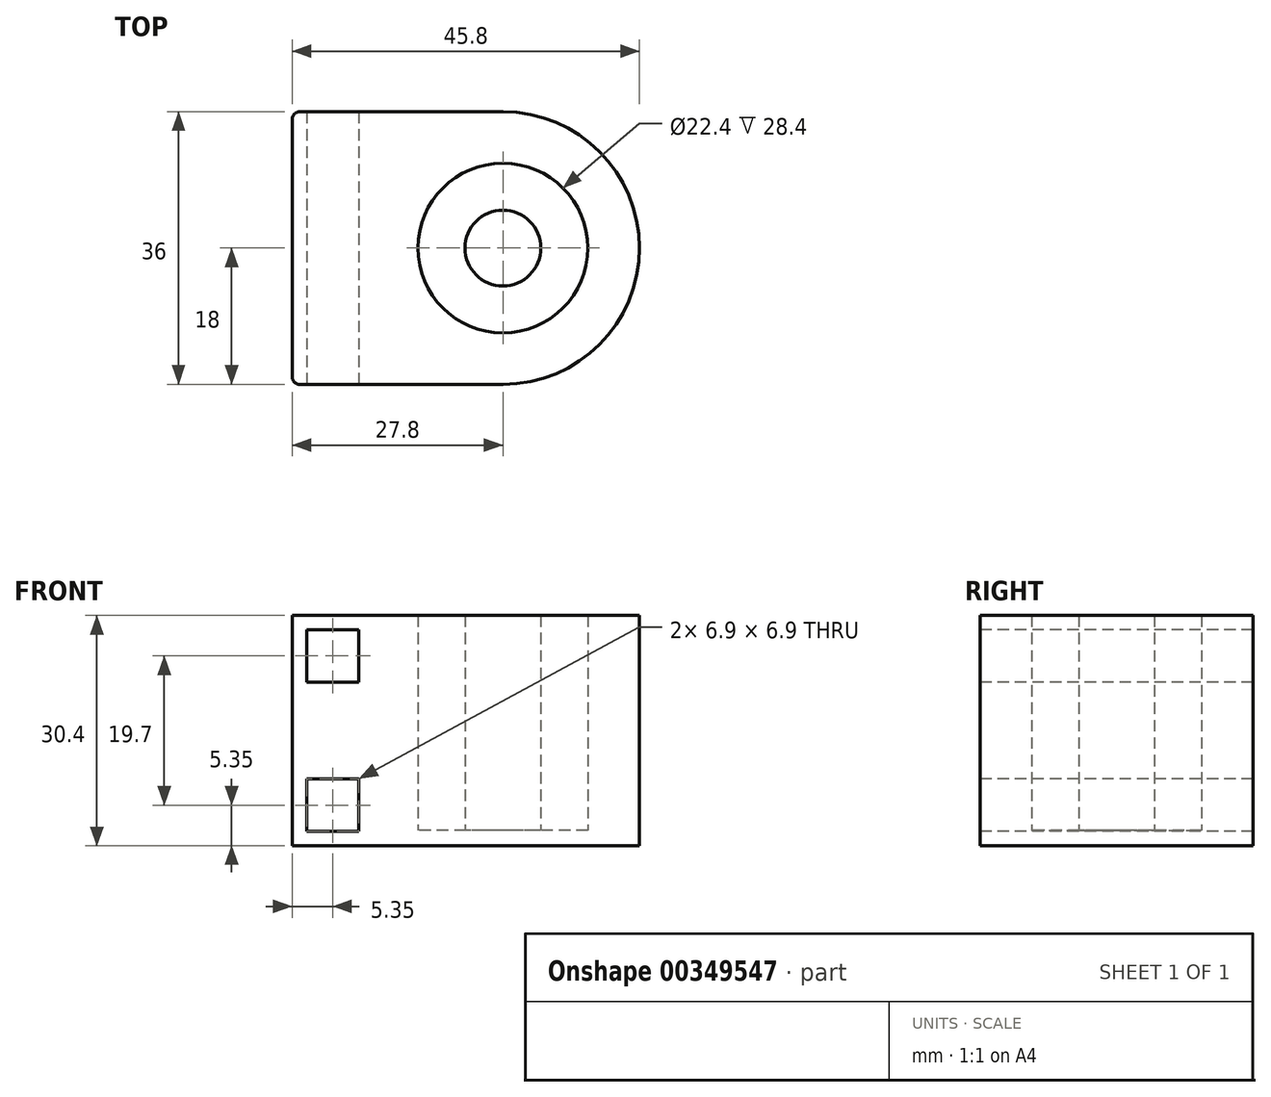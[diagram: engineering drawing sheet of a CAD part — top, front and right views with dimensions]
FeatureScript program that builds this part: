
annotation { "Feature Type Name" : "Feature", "Feature Type Description" : "" }
export const myFeature = defineFeature(function(context is Context, id is Id, definition is map)
    precondition{}
    {
        {
            var Q0;
            Q0=qCreatedBy(makeId("Top.planeOp"),FACE);
            var sketch = newSketch(context, id + "F0", { "sketchPlane" : qUnion([Q0])});
            skCircle(sketch, "E0", {"center": v(0, 0) * mm, "radius": 11.2 * mm});
            skCircle(sketch, "E1", {"center": v(0, 0) * mm, "radius": 18 * mm});
            skLineSegment(sketch, "E2", {"start": v(0, 0) * mm, "end": v(0, 18) * mm});
            skLineSegment(sketch, "E3.bottom", {"start": v(0, 18) * mm, "end": v(-27.8, 18) * mm});
            skLineSegment(sketch, "E3.top", {"start": v(0, -18) * mm, "end": v(-27.8, -18) * mm});
            skLineSegment(sketch, "E3.left", {"start": v(0, 18) * mm, "end": v(0, -18) * mm});
            skLineSegment(sketch, "E3.right", {"start": v(-27.8, 18) * mm, "end": v(-27.8, -18) * mm});
            skCircle(sketch, "E4", {"center": v(0, 0) * mm, "radius": 5 * mm});
            skSolve(sketch);
        }
        {
            var Q0;
            {var subQ1=sQuery(id+"F0.wireOp",EDGE,"E3.bottom");Q0=makeQuery(id+"F0.imprint","IMPRINT",FACE,{"disambiguationData":[TD([[makeQuery(id+"F0.imprint","IMPRINT",EDGE,{"derivedFrom":subQ1}),1.0]])]});}
            var Q1;
            {var subQ0=sQuery(id+"F0.wireOp",EDGE,"E3.left");var subQ1=sQuery(id+"F0.wireOp",EDGE,"E0");var subQ2=makeQuery(id+"F0.imprint","INTERSECT",VERTEX,{"disambiguationData":[OD(0.0)],"derivedFrom":[subQ1,subQ0]});Q1=makeQuery(id+"F0.imprint","IMPRINT",FACE,{"disambiguationData":[TD([[makeQuery(id+"F0.imprint","IMPRINT",EDGE,{"disambiguationData":[TD([[subQ2,-1.0]])],"derivedFrom":subQ1}),-1.0]])]});}
            var Q2;
            {var subQ0=sQuery(id+"F0.wireOp",EDGE,"E3.left");var subQ1=sQuery(id+"F0.wireOp",EDGE,"E0");var subQ2=makeQuery(id+"F0.imprint","INTERSECT",VERTEX,{"disambiguationData":[OD(0.0)],"derivedFrom":[subQ1,subQ0]});Q2=makeQuery(id+"F0.imprint","IMPRINT",FACE,{"disambiguationData":[TD([[makeQuery(id+"F0.imprint","IMPRINT",EDGE,{"disambiguationData":[TD([[subQ2,1.0]])],"derivedFrom":subQ1}),-1.0]])]});}
            extrude(context, id + "F1", {"entities" : qUnion([Q0, Q1, Q2]), "depth" : 30.4 * mm});
        }
        {
            var Q0;
            {var subQ5=sQuery(id+"F0.wireOp",EDGE,"E3.left");var subQ6=sQuery(id+"F0.wireOp",EDGE,"E0");var subQ7=makeQuery(id+"F0.imprint","INTERSECT",VERTEX,{"disambiguationData":[OD(0.0)],"derivedFrom":[subQ6,subQ5]});Q0=makeQuery(id+"F0.imprint","IMPRINT",FACE,{"disambiguationData":[TD([[makeQuery(id+"F0.imprint","IMPRINT",EDGE,{"disambiguationData":[TD([[subQ7,1.0]])],"derivedFrom":subQ6}),1.0]])]});}
            var Q1;
            {var subQ12=sQuery(id+"F0.wireOp",EDGE,"E3.left");var subQ13=sQuery(id+"F0.wireOp",EDGE,"E0");var subQ14=makeQuery(id+"F0.imprint","INTERSECT",VERTEX,{"disambiguationData":[OD(0.0)],"derivedFrom":[subQ13,subQ12]});Q1=makeQuery(id+"F0.imprint","IMPRINT",FACE,{"disambiguationData":[TD([[makeQuery(id+"F0.imprint","IMPRINT",EDGE,{"disambiguationData":[TD([[subQ14,-1.0]])],"derivedFrom":subQ13}),1.0]])]});}
            var Q2;
            {var subQ0=sQuery(id+"F0.wireOp",EDGE,"8lIcankL-Q5gj-hwWK-AL3X-qkDdrb8kB20Y");var subQ1=sQuery(id+"F0.wireOp",EDGE,"E3.left");var subQ2=makeQuery(id+"F0.imprint","INTERSECT",VERTEX,{"disambiguationData":[OD(1.0)],"derivedFrom":[subQ1,subQ0]});Q2=makeQuery(id+"F0.imprint","IMPRINT",FACE,{"disambiguationData":[TD([[makeQuery(id+"F0.imprint","IMPRINT",EDGE,{"disambiguationData":[TD([[subQ2,-1.0]])],"derivedFrom":subQ1}),-1.0]])]});}
            var Q3;
            {var subQ0=sQuery(id+"F0.wireOp",EDGE,"8lIcankL-Q5gj-hwWK-AL3X-qkDdrb8kB20Y");var subQ1=sQuery(id+"F0.wireOp",EDGE,"E3.left");var subQ2=makeQuery(id+"F0.imprint","INTERSECT",VERTEX,{"disambiguationData":[OD(1.0)],"derivedFrom":[subQ1,subQ0]});Q3=makeQuery(id+"F0.imprint","IMPRINT",FACE,{"disambiguationData":[TD([[makeQuery(id+"F0.imprint","IMPRINT",EDGE,{"disambiguationData":[TD([[subQ2,-1.0]])],"derivedFrom":subQ1}),1.0]])]});}
            var Q4;
            {var subQ0=sQuery(id+"F0.wireOp",EDGE,"acbbde6d-6b89-4c3b-ba40-6ba3c0975178.1");var subQ1=sQuery(id+"F0.wireOp",EDGE,"E4");var subQ2=makeQuery(id+"F0.imprint","INTERSECT",VERTEX,{"disambiguationData":[OD(1.0)],"derivedFrom":[subQ1,subQ0]});Q4=makeQuery(id+"F0.imprint","IMPRINT",FACE,{"disambiguationData":[TD([[makeQuery(id+"F0.imprint","IMPRINT",EDGE,{"disambiguationData":[TD([[subQ2,-1.0]])],"derivedFrom":subQ1}),-1.0]])]});}
            var Q5;
            {var subQ0=sQuery(id+"F0.wireOp",EDGE,"acbbde6d-6b89-4c3b-ba40-6ba3c0975178.2");var subQ1=sQuery(id+"F0.wireOp",EDGE,"E4");var subQ2=makeQuery(id+"F0.imprint","INTERSECT",VERTEX,{"disambiguationData":[OD(1.0)],"derivedFrom":[subQ1,subQ0]});Q5=makeQuery(id+"F0.imprint","IMPRINT",FACE,{"disambiguationData":[TD([[makeQuery(id+"F0.imprint","IMPRINT",EDGE,{"disambiguationData":[TD([[subQ2,1.0]])],"derivedFrom":subQ1}),-1.0]])]});}
            var Q6;
            {var subQ0=sQuery(id+"F0.wireOp",EDGE,"E4");var subQ1=sQuery(id+"F0.wireOp",EDGE,"E3.left");var subQ2=makeQuery(id+"F0.imprint","INTERSECT",VERTEX,{"disambiguationData":[OD(1.0)],"derivedFrom":[subQ1,subQ0]});Q6=makeQuery(id+"F0.imprint","IMPRINT",FACE,{"disambiguationData":[TD([[makeQuery(id+"F0.imprint","IMPRINT",EDGE,{"disambiguationData":[TD([[subQ2,-1.0]])],"derivedFrom":subQ1}),1.0]])]});}
            var Q7;
            {var subQ0=sQuery(id+"F0.wireOp",EDGE,"E4");var subQ1=sQuery(id+"F0.wireOp",EDGE,"E3.left");var subQ2=makeQuery(id+"F0.imprint","INTERSECT",VERTEX,{"disambiguationData":[OD(1.0)],"derivedFrom":[subQ1,subQ0]});Q7=makeQuery(id+"F0.imprint","IMPRINT",FACE,{"disambiguationData":[TD([[makeQuery(id+"F0.imprint","IMPRINT",EDGE,{"disambiguationData":[TD([[subQ2,-1.0]])],"derivedFrom":subQ1}),-1.0]])]});}
            extrude(context, id + "F2", {"entities" : qUnion([Q0, Q1, Q2, Q3, Q4, Q5, Q6, Q7]), "operationType" : NewBodyOperationType.ADD, "depth" : 2 * mm});
        }
        {
            var Q0;
            Q0=makeQuery(id+"F1.opExtrude","SWEPT_FACE",FACE,{"disambiguationData":[OSD([sQuery(id+"F0.wireOp",EDGE,"E3.top")])]});
            var sketch = newSketch(context, id + "F3", { "sketchPlane" : qUnion([Q0])});
            skLineSegment(sketch, "E5.bottom", {"start": v(-27.8, 30.4) * mm, "end": v(-25.9, 30.4) * mm});
            skLineSegment(sketch, "E5.top", {"start": v(-27.8, 28.5) * mm, "end": v(-25.9, 28.5) * mm});
            skLineSegment(sketch, "E5.left", {"start": v(-27.8, 30.4) * mm, "end": v(-27.8, 28.5) * mm});
            skLineSegment(sketch, "E5.right", {"start": v(-25.9, 30.4) * mm, "end": v(-25.9, 28.5) * mm});
            skLineSegment(sketch, "E6.bottom", {"start": v(-25.9, 28.5) * mm, "end": v(-19, 28.5) * mm});
            skLineSegment(sketch, "E6.top", {"start": v(-25.9, 21.6) * mm, "end": v(-19, 21.6) * mm});
            skLineSegment(sketch, "E6.left", {"start": v(-25.9, 28.5) * mm, "end": v(-25.9, 21.6) * mm});
            skLineSegment(sketch, "E6.right", {"start": v(-19, 28.5) * mm, "end": v(-19, 21.6) * mm});
            skPoint(sketch, "E7", {"position": v(-27.8, 15.2) * mm});
            skLineSegment(sketch, "E8", {"start": v(-27.8, 15.2) * mm, "end": v(0, 15.2) * mm});
            skLineSegment(sketch, "E9.MirrorCS", {"start": v(-25.9, 8.8) * mm, "end": v(-19, 8.8) * mm});
            skLineSegment(sketch, "E10.MirrorCS", {"start": v(-19, 1.9) * mm, "end": v(-19, 8.8) * mm});
            skLineSegment(sketch, "E11.MirrorCS", {"start": v(-25.9, 1.9) * mm, "end": v(-19, 1.9) * mm});
            skLineSegment(sketch, "E12.MirrorCS", {"start": v(-25.9, 1.9) * mm, "end": v(-25.9, 8.8) * mm});
            skSolve(sketch);
        }
        {
            var Q0;
            Q0=makeQuery(id+"F3.imprint","IMPRINT",FACE,{"disambiguationData":[TD([[makeQuery(id+"F3.imprint","IMPRINT",EDGE,{"derivedFrom":sQuery(id+"F3.wireOp",EDGE,"E6.bottom")}),-1.0]])]});
            var Q1;
            Q1=makeQuery(id+"F3.imprint","IMPRINT",FACE,{"disambiguationData":[TD([[makeQuery(id+"F3.imprint","IMPRINT",EDGE,{"derivedFrom":sQuery(id+"F3.wireOp",EDGE,"E9.MirrorCS")}),-1.0]])]});
            extrude(context, id + "F4", {"entities" : qUnion([Q0, Q1]), "operationType" : NewBodyOperationType.REMOVE, "oppositeDirection" : true, "depth" : 50 * mm});
        }
        {
            var Q0;
            Q0=makeQuery(id+"F1.opExtrude","SWEPT_EDGE",EDGE,{"disambiguationData":[OSD([sQuery(id+"F0.wireOp",EDGE,"E3.bottom"),sQuery(id+"F0.wireOp",EDGE,"E3.right")])]});
            var Q1;
            Q1=makeQuery(id+"F1.opExtrude","SWEPT_EDGE",EDGE,{"disambiguationData":[OSD([sQuery(id+"F0.wireOp",EDGE,"E3.top"),sQuery(id+"F0.wireOp",EDGE,"E3.right")])]});
            fillet(context, id + "F5", {"entities" : qUnion([Q0, Q1]), "radius" : 1 * mm, "tangentPropagation" : true, "allowEdgeOverflow" : false});
        }
        {
            var Q0;
            {var subQ0=sQuery(id+"F0.wireOp",EDGE,"H9ivOdNi-cplr-VCbd-cNgX-2CwGjbdZF1iG");var subQ1=sQuery(id+"F0.wireOp",EDGE,"E3.left");var subQ2=makeQuery(id+"F0.imprint","INTERSECT",VERTEX,{"disambiguationData":[OD(0.0)],"derivedFrom":[subQ1,subQ0]});Q0=makeQuery(id+"F0.imprint","IMPRINT",FACE,{"disambiguationData":[TD([[makeQuery(id+"F0.imprint","IMPRINT",EDGE,{"disambiguationData":[TD([[subQ2,-1.0]])],"derivedFrom":subQ1}),-1.0]])]});}
            var Q1;
            {var subQ0=sQuery(id+"F0.wireOp",EDGE,"H9ivOdNi-cplr-VCbd-cNgX-2CwGjbdZF1iG");var subQ1=sQuery(id+"F0.wireOp",EDGE,"E3.left");var subQ2=makeQuery(id+"F0.imprint","INTERSECT",VERTEX,{"disambiguationData":[OD(0.0)],"derivedFrom":[subQ1,subQ0]});Q1=makeQuery(id+"F0.imprint","IMPRINT",FACE,{"disambiguationData":[TD([[makeQuery(id+"F0.imprint","IMPRINT",EDGE,{"disambiguationData":[TD([[subQ2,-1.0]])],"derivedFrom":subQ1}),1.0]])]});}
            var Q2;
            Q2=makeQuery(id+"F1.opExtrude","CAP_FACE",FACE,{"disambiguationData":[OSD([sQuery(id+"F0.wireOp",EDGE,"E0"),sQuery(id+"F0.wireOp",EDGE,"E1"),sQuery(id+"F0.wireOp",EDGE,"E3.bottom"),sQuery(id+"F0.wireOp",EDGE,"E3.top"),sQuery(id+"F0.wireOp",EDGE,"E3.right")])],"isStart":false});
            extrude(context, id + "F6", {"entities" : qUnion([Q0, Q1]), "operationType" : NewBodyOperationType.ADD, "endBound" : BoundingType.UP_TO_SURFACE, "endBoundEntityFace" : qUnion([Q2]), "depth" : 25 * mm});
        }
    });
